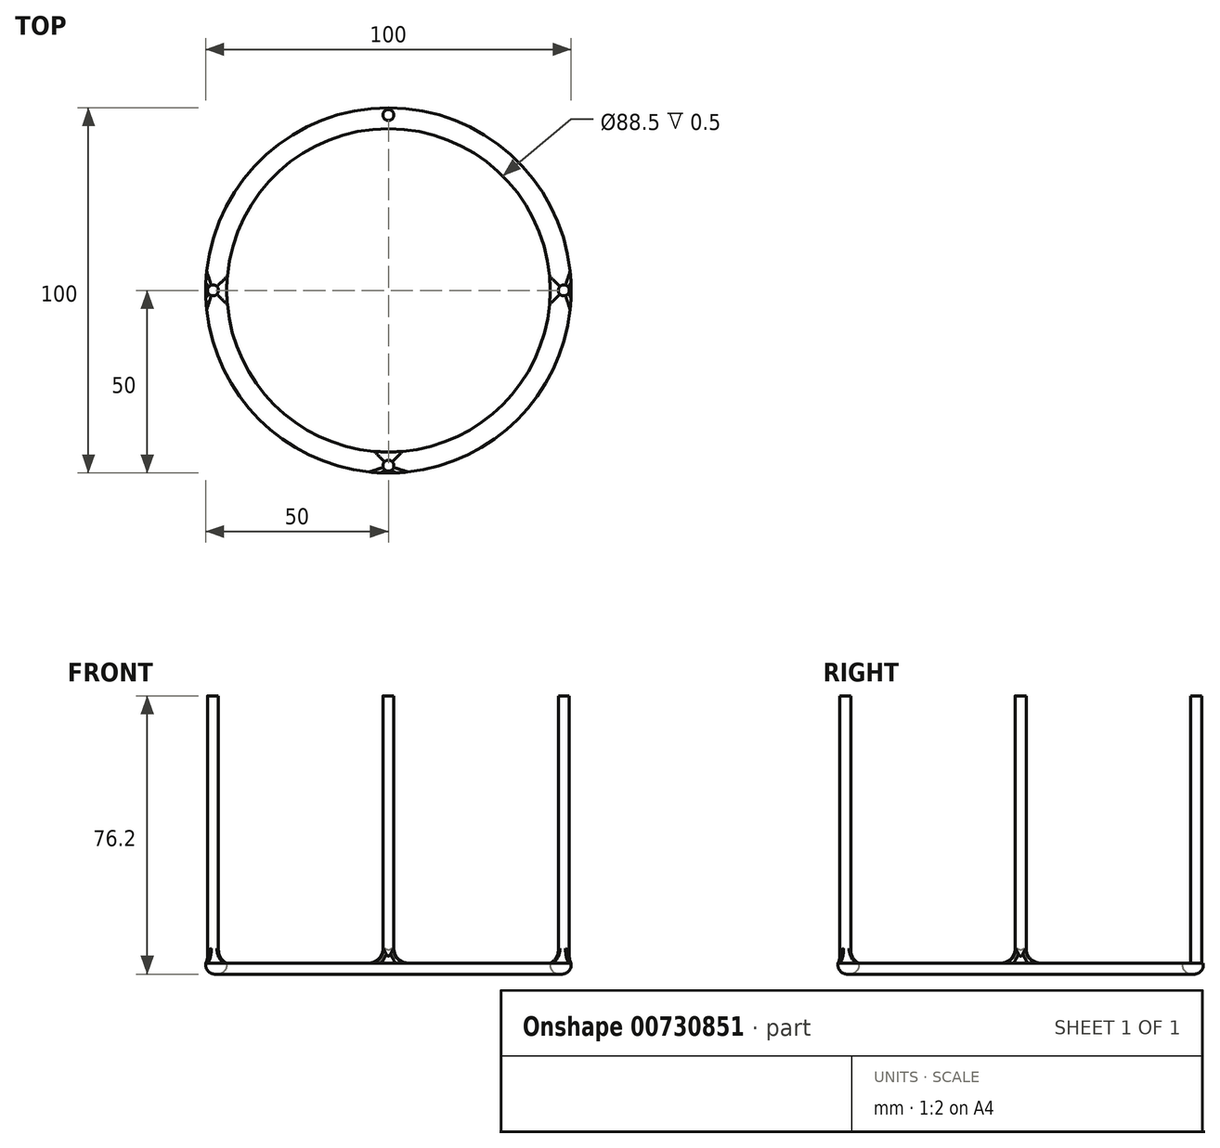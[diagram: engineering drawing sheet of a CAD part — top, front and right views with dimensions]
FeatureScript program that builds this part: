
annotation { "Feature Type Name" : "Feature", "Feature Type Description" : "" }
export const myFeature = defineFeature(function(context is Context, id is Id, definition is map)
    precondition{}
    {
        {
            var Q0;
            Q0=qCreatedBy(makeId("Front.planeOp"),FACE);
            var sketch = newSketch(context, id + "F0", { "sketchPlane" : qUnion([Q0])});
            skLineSegment(sketch, "E0", {"start": v(0, 69.46) * mm, "end": v(0, -56.9) * mm});
            skSolve(sketch);
        }
        {
            var Q0;
            Q0=qCreatedBy(makeId("Top.planeOp"),FACE);
            var sketch = newSketch(context, id + "F1", { "sketchPlane" : qUnion([Q0])});
            skCircle(sketch, "E1", {"center": v(0, 48) * mm, "radius": 1.5 * mm});
            skCircle(sketch, "E2.1.0", {"center": v(-48, 0) * mm, "radius": 1.5 * mm});
            skCircle(sketch, "E2.2.0", {"center": v(0, -48) * mm, "radius": 1.5 * mm});
            skPoint(sketch, "E2.center", {"position": v(0, 0) * mm});
            skCircle(sketch, "E3", {"center": v(0, 0) * mm, "radius": 50 * mm});
            skCircle(sketch, "E4", {"center": v(0, 0) * mm, "radius": 46 * mm});
            skCircle(sketch, "E5.1.3.0", {"center": v(48, 0) * mm, "radius": 1.5 * mm});
            skSolve(sketch);
        }
        {
            var Q0;
            Q0=makeQuery(id+"F1.imprint","IMPRINT",FACE,{"disambiguationData":[TD([[makeQuery(id+"F1.imprint","IMPRINT",EDGE,{"derivedFrom":sQuery(id+"F1.wireOp",EDGE,"E1")}),1.0]])]});
            var Q1;
            Q1=makeQuery(id+"F1.imprint","IMPRINT",FACE,{"disambiguationData":[TD([[makeQuery(id+"F1.imprint","IMPRINT",EDGE,{"derivedFrom":sQuery(id+"F1.wireOp",EDGE,"E2.2.0")}),1.0]])]});
            var Q2;
            Q2=makeQuery(id+"F1.imprint","IMPRINT",FACE,{"disambiguationData":[TD([[makeQuery(id+"F1.imprint","IMPRINT",EDGE,{"derivedFrom":sQuery(id+"F1.wireOp",EDGE,"E2.1.0")}),1.0]])]});
            var Q3;
            Q3=makeQuery(id+"F1.imprint","IMPRINT",FACE,{"disambiguationData":[TD([[makeQuery(id+"F1.imprint","IMPRINT",EDGE,{"derivedFrom":sQuery(id+"F1.wireOp",EDGE,"E5.1.3.0")}),1.0]])]});
            extrude(context, id + "F2", {"entities" : qUnion([Q0, Q1, Q2, Q3]), "depth" : 76.2 * mm, "offsetDistance" : 25 * mm});
        }
        {
            var Q0;
            Q0=makeQuery(id+"F2.opExtrude","CAP_FACE",FACE,{"disambiguationData":[OSD([sQuery(id+"F1.wireOp",EDGE,"E1")])],"isStart":true});
            var sketch = newSketch(context, id + "F3", { "sketchPlane" : qUnion([Q0])});
            skCircle(sketch, "E6", {"center": v(0, 0) * mm, "radius": 50 * mm});
            skCircle(sketch, "E7", {"center": v(0, 0) * mm, "radius": 46 * mm});
            skSolve(sketch);
        }
        {
            var Q0;
            Q0=makeQuery(id+"F3.imprint","IMPRINT",FACE,{"disambiguationData":[TD([[makeQuery(id+"F3.imprint","IMPRINT",EDGE,{"derivedFrom":sQuery(id+"F3.wireOp",EDGE,"E7")}),1.0]])]});
            var Q1;
            Q1=makeQuery(id+"F3.imprint","IMPRINT",FACE,{"disambiguationData":[TD([[makeQuery(id+"F3.imprint","IMPRINT",EDGE,{"derivedFrom":sQuery(id+"F3.wireOp",EDGE,"E6")}),1.0]])]});
            var Q2;
            Q2=sQuery(id+"F3.wireOp",EDGE,"E6");
            var Q3;
            Q3=sQuery(id+"F3.wireOp",EDGE,"E7");
            extrude(context, id + "F4", {"entities" : qUnion([Q0, Q1]), "surfaceEntities" : qUnion([Q2, Q3]), "oppositeDirection" : true, "depth" : 3 * mm, "offsetDistance" : 25 * mm});
        }
        {
            var Q0;
            {var subQ0=sQuery(id+"F1.wireOp",EDGE,"E1");Q0=makeQuery(id+"FhonZYvOEkIcrAR_4.opBoolean","MERGE",FACE,{"derivedFrom":[makeQuery(id+"F2.opExtrude","CAP_FACE",FACE,{"disambiguationData":[OSD([subQ0])],"isStart":true}),makeQuery(id+"F2.opExtrude","CAP_FACE",FACE,{"disambiguationData":[OSD([sQuery(id+"F1.wireOp",EDGE,"E2.1.0")])],"isStart":true}),makeQuery(id+"F2.opExtrude","CAP_FACE",FACE,{"disambiguationData":[OSD([sQuery(id+"F1.wireOp",EDGE,"E2.2.0")])],"isStart":true}),makeQuery(id+"F4.opExtrude","CAP_FACE",FACE,{"disambiguationData":[OSD([subQ0,sQuery(id+"F3.wireOp",EDGE,"E6")])],"isStart":true})]});}
            var sketch = newSketch(context, id + "F5", { "sketchPlane" : qUnion([Q0])});
            skPoint(sketch, "E8", {"position": v(0, 0) * mm});
            skSolve(sketch);
        }
        {
            var Q0;
            Q0=makeQuery(id+"F2.opExtrude","SWEPT_BODY",BODY,{"disambiguationData":[OSD([sQuery(id+"F1.wireOp",EDGE,"E2.2.0")])]});
            var Q1;
            Q1=makeQuery(id+"F2.opExtrude","SWEPT_BODY",BODY,{"disambiguationData":[OSD([sQuery(id+"F1.wireOp",EDGE,"E5.1.3.0")])]});
            var Q2;
            Q2=makeQuery(id+"F2.opExtrude","SWEPT_BODY",BODY,{"disambiguationData":[OSD([sQuery(id+"F1.wireOp",EDGE,"E1")])]});
            var Q3;
            Q3=makeQuery(id+"F4.opExtrude","SWEPT_BODY",BODY,{"disambiguationData":[OSD([sQuery(id+"F1.wireOp",EDGE,"E1"),sQuery(id+"F3.wireOp",EDGE,"E6")])]});
            var Q4;
            Q4=makeQuery(id+"F2.opExtrude","SWEPT_BODY",BODY,{"disambiguationData":[OSD([sQuery(id+"F1.wireOp",EDGE,"E2.1.0")])]});
            booleanBodies(context, id + "F6", {"operationType" : BooleanOperationType.UNION, "tools" : qUnion([Q0, Q1, Q2, Q3, Q4])});
        }
        {
            var Q0;
            Q0=sQuery(id+"F5.wireOp",VERTEX,"E8");
            var Q1;
            Q1=makeQuery(id+"F2.opExtrude","SWEPT_BODY",BODY,{"disambiguationData":[OSD([sQuery(id+"F1.wireOp",EDGE,"E2.2.0")])]});
            hole(context, id + "F7", {"style" : HoleStyle.SIMPLE, "endStyle" : HoleEndStyle.THROUGH, "holeDiameter" : 88.5 * mm, "majorDiameter" : 5 * mm, "isTappedThrough" : true, "tappedDepth" : 12 * mm, "tapClearance" : 3, "locations" : qUnion([Q0]), "scope" : qUnion([Q1])});
        }
        {
            var Q0;
            Q0=makeQuery(id+"F6.opBoolean","INTERSECT",EDGE,{"derivedFrom":[makeQuery(id+"F2.opExtrude","SWEPT_FACE",FACE,{"disambiguationData":[OSD([sQuery(id+"F1.wireOp",EDGE,"E5.1.3.0")])]}),makeQuery(id+"F4.opExtrude","CAP_FACE",FACE,{"disambiguationData":[OSD([sQuery(id+"F1.wireOp",EDGE,"E1"),sQuery(id+"F3.wireOp",EDGE,"E6")])],"isStart":false})]});
            var Q1;
            Q1=makeQuery(id+"F4.opExtrude","CAP_EDGE",EDGE,{"disambiguationData":[OSD([sQuery(id+"F1.wireOp",EDGE,"E1")])],"isStart":false});
            var Q2;
            Q2=makeQuery(id+"F6.opBoolean","INTERSECT",EDGE,{"derivedFrom":[makeQuery(id+"F2.opExtrude","SWEPT_FACE",FACE,{"disambiguationData":[OSD([sQuery(id+"F1.wireOp",EDGE,"E2.1.0")])]}),makeQuery(id+"F4.opExtrude","CAP_FACE",FACE,{"disambiguationData":[OSD([sQuery(id+"F1.wireOp",EDGE,"E1"),sQuery(id+"F3.wireOp",EDGE,"E6")])],"isStart":false})]});
            var Q3;
            Q3=makeQuery(id+"F6.opBoolean","INTERSECT",EDGE,{"derivedFrom":[makeQuery(id+"F2.opExtrude","SWEPT_FACE",FACE,{"disambiguationData":[OSD([sQuery(id+"F1.wireOp",EDGE,"E2.2.0")])]}),makeQuery(id+"F4.opExtrude","CAP_FACE",FACE,{"disambiguationData":[OSD([sQuery(id+"F1.wireOp",EDGE,"E1"),sQuery(id+"F3.wireOp",EDGE,"E6")])],"isStart":false})]});
            fillet(context, id + "F8", {"entities" : qUnion([Q0, Q1, Q2, Q3]), "radius" : 4 * mm, "tangentPropagation" : true, "allowEdgeOverflow" : false});
        }
        {
            var Q0;
            Q0=makeQuery(id+"F7.hole-0.boolean.opBoolean","COPY",EDGE,{"derivedFrom":makeQuery(id+"F7.hole-0.opRevolve","SWEPT_EDGE",EDGE,{"disambiguationData":[OSD([sQuery(id+"F7.hole-0.sketch.wireOp",EDGE,"core_line_2"),sQuery(id+"F7.hole-0.sketch.wireOp",EDGE,"core_line_3")])]})});
            var Q1;
            Q1=makeQuery(id+"F4.opExtrude","CAP_EDGE",EDGE,{"disambiguationData":[OSD([sQuery(id+"F3.wireOp",EDGE,"E6")])],"isStart":true});
            var Q2;
            {var subQ0=sQuery(id+"F1.wireOp",EDGE,"E1");Q2=makeQuery(id+"F6.opBoolean","MERGE",FACE,{"derivedFrom":[makeQuery(id+"F2.opExtrude","CAP_FACE",FACE,{"disambiguationData":[OSD([subQ0])],"isStart":true}),makeQuery(id+"F2.opExtrude","CAP_FACE",FACE,{"disambiguationData":[OSD([sQuery(id+"F1.wireOp",EDGE,"E2.2.0")])],"isStart":true}),makeQuery(id+"F2.opExtrude","CAP_FACE",FACE,{"disambiguationData":[OSD([sQuery(id+"F1.wireOp",EDGE,"E5.1.3.0")])],"isStart":true}),makeQuery(id+"F4.opExtrude","CAP_FACE",FACE,{"disambiguationData":[OSD([subQ0,sQuery(id+"F3.wireOp",EDGE,"E6")])],"isStart":true})]});}
            fillet(context, id + "F9", {"entities" : qUnion([Q0, Q1, Q2]), "radius" : 2.5 * mm, "tangentPropagation" : true, "allowEdgeOverflow" : false});
        }
    });
